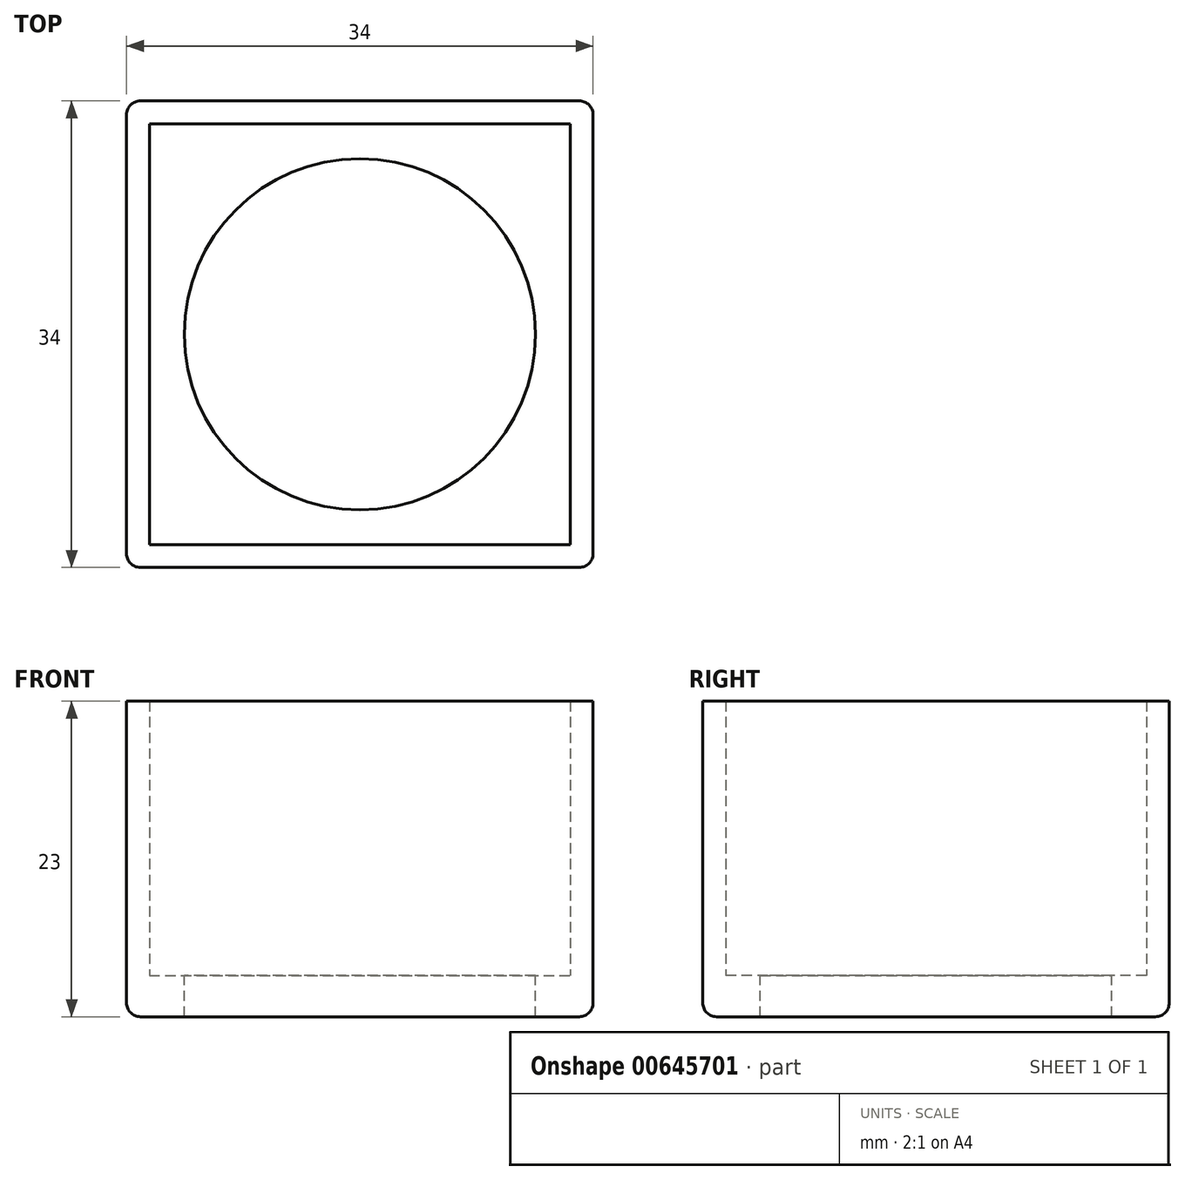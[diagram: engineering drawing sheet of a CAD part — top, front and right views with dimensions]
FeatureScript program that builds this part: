
annotation { "Feature Type Name" : "Feature", "Feature Type Description" : "" }
export const myFeature = defineFeature(function(context is Context, id is Id, definition is map)
    precondition{}
    {
        {
            var Q0;
            Q0=qCreatedBy(makeId("Top.planeOp"),FACE);
            var sketch = newSketch(context, id + "F0", { "sketchPlane" : qUnion([Q0])});
            skCircle(sketch, "E0", {"center": v(0, 0) * mm, "radius": 12.8 * mm});
            skLineSegment(sketch, "E1.bottom", {"start": v(-17, 17) * mm, "end": v(17, 17) * mm});
            skLineSegment(sketch, "E1.top", {"start": v(-17, -17) * mm, "end": v(17, -17) * mm});
            skLineSegment(sketch, "E1.left", {"start": v(-17, 17) * mm, "end": v(-17, -17) * mm});
            skLineSegment(sketch, "E1.right", {"start": v(17, 17) * mm, "end": v(17, -17) * mm});
            skLineSegment(sketch, "E2.bottom", {"start": v(-15.34, 15.34) * mm, "end": v(15.34, 15.34) * mm});
            skLineSegment(sketch, "E2.top", {"start": v(-15.34, -15.34) * mm, "end": v(15.33, -15.34) * mm});
            skLineSegment(sketch, "E2.left", {"start": v(-15.33, 15.34) * mm, "end": v(-15.34, -15.34) * mm});
            skLineSegment(sketch, "E2.right", {"start": v(15.34, 15.34) * mm, "end": v(15.33, -15.33) * mm});
            skCircle(sketch, "E3", {"center": v(0, 0) * mm, "radius": 14.3 * mm});
            skSolve(sketch);
        }
        {
            var Q0;
            Q0=makeQuery(id+"F0.imprint","IMPRINT",FACE,{"disambiguationData":[TD([[makeQuery(id+"F0.imprint","IMPRINT",EDGE,{"derivedFrom":sQuery(id+"F0.wireOp",EDGE,"E1.bottom")}),-1.0]])]});
            var Q1;
            Q1=makeQuery(id+"F0.imprint","IMPRINT",FACE,{"disambiguationData":[TD([[makeQuery(id+"F0.imprint","IMPRINT",EDGE,{"derivedFrom":sQuery(id+"F0.wireOp",EDGE,"E0")}),-1.0]])]});
            var Q2;
            Q2=makeQuery(id+"F0.imprint","IMPRINT",FACE,{"disambiguationData":[TD([[makeQuery(id+"F0.imprint","IMPRINT",EDGE,{"derivedFrom":sQuery(id+"F0.wireOp",EDGE,"E2.bottom")}),-1.0]])]});
            extrude(context, id + "F1", {"entities" : qUnion([Q0, Q1, Q2]), "oppositeDirection" : true, "depth" : 3 * mm, "offsetDistance" : 25 * mm});
        }
        {
            var Q0;
            Q0=makeQuery(id+"F0.imprint","IMPRINT",FACE,{"disambiguationData":[TD([[makeQuery(id+"F0.imprint","IMPRINT",EDGE,{"derivedFrom":sQuery(id+"F0.wireOp",EDGE,"E1.bottom")}),-1.0]])]});
            extrude(context, id + "F2", {"entities" : qUnion([Q0]), "operationType" : NewBodyOperationType.ADD, "depth" : 20 * mm, "offsetDistance" : 25 * mm});
        }
        {
            var Q0;
            Q0=makeQuery(id+"F1.opExtrude","CAP_EDGE",EDGE,{"disambiguationData":[OSD([sQuery(id+"F0.wireOp",EDGE,"E1.right")])],"isStart":false});
            var Q1;
            Q1=makeQuery(id+"F1.opExtrude","CAP_EDGE",EDGE,{"disambiguationData":[OSD([sQuery(id+"F0.wireOp",EDGE,"E1.bottom")])],"isStart":false});
            var Q2;
            Q2=makeQuery(id+"F1.opExtrude","CAP_EDGE",EDGE,{"disambiguationData":[OSD([sQuery(id+"F0.wireOp",EDGE,"E1.left")])],"isStart":false});
            var Q3;
            Q3=makeQuery(id+"F1.opExtrude","CAP_EDGE",EDGE,{"disambiguationData":[OSD([sQuery(id+"F0.wireOp",EDGE,"E1.top")])],"isStart":false});
            var Q4;
            {var subQ0=sQuery(id+"F0.wireOp",EDGE,"E1.right");var subQ1=sQuery(id+"F0.wireOp",EDGE,"E1.top");Q4=makeQuery(id+"F2.boolean.opBoolean","MERGE",EDGE,{"derivedFrom":[makeQuery(id+"F1.opExtrude","SWEPT_EDGE",EDGE,{"disambiguationData":[OSD([subQ1,subQ0])]}),makeQuery(id+"F2.opExtrude","SWEPT_EDGE",EDGE,{"disambiguationData":[OSD([subQ1,subQ0])]})]});}
            var Q5;
            {var subQ0=sQuery(id+"F0.wireOp",EDGE,"E1.right");var subQ1=sQuery(id+"F0.wireOp",EDGE,"E1.bottom");Q5=makeQuery(id+"F2.boolean.opBoolean","MERGE",EDGE,{"derivedFrom":[makeQuery(id+"F1.opExtrude","SWEPT_EDGE",EDGE,{"disambiguationData":[OSD([subQ1,subQ0])]}),makeQuery(id+"F2.opExtrude","SWEPT_EDGE",EDGE,{"disambiguationData":[OSD([subQ1,subQ0])]})]});}
            var Q6;
            {var subQ0=sQuery(id+"F0.wireOp",EDGE,"E1.left");var subQ1=sQuery(id+"F0.wireOp",EDGE,"E1.bottom");Q6=makeQuery(id+"F2.boolean.opBoolean","MERGE",EDGE,{"derivedFrom":[makeQuery(id+"F1.opExtrude","SWEPT_EDGE",EDGE,{"disambiguationData":[OSD([subQ1,subQ0])]}),makeQuery(id+"F2.opExtrude","SWEPT_EDGE",EDGE,{"disambiguationData":[OSD([subQ1,subQ0])]})]});}
            var Q7;
            {var subQ0=sQuery(id+"F0.wireOp",EDGE,"E1.left");var subQ1=sQuery(id+"F0.wireOp",EDGE,"E1.top");Q7=makeQuery(id+"F2.boolean.opBoolean","MERGE",EDGE,{"derivedFrom":[makeQuery(id+"F1.opExtrude","SWEPT_EDGE",EDGE,{"disambiguationData":[OSD([subQ1,subQ0])]}),makeQuery(id+"F2.opExtrude","SWEPT_EDGE",EDGE,{"disambiguationData":[OSD([subQ1,subQ0])]})]});}
            fillet(context, id + "F3", {"entities" : qUnion([Q0, Q1, Q2, Q3, Q4, Q5, Q6, Q7]), "radius" : 1 * mm, "tangentPropagation" : true, "allowEdgeOverflow" : false});
        }
    });
